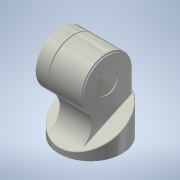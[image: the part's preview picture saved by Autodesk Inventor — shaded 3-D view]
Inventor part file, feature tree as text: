
AUTODESK INVENTOR PART (.ipt)
format: ipt  version: 2021 (Build 250183000, 183)  size: 448,512 bytes
history: native  units: mm (DEFAULTED — no unit token found)
features: sketch x9, extrude x5, hole x2, other x1, fillet x1, mirror x1, shell x1, revolve x1, pattern_circular x1
ambient origin geometry x8: Origin, YZ Plane, XZ Plane, XY Plane, X Axis, Y Axis, Z Axis, Center Point
bodies: Solid1 (feature_tree)
feature tree (22):
  other  "Center-Work Plane"
  fillet  "Chamfer"  Radius=150.0mm
  sketch  "Sketch6"  dims[d1=120.0mm d2=0.0mm d7=13.0mm d8=4.363323mm]
  extrude  "Extrusion6"  Depth=13.0mm
  mirror  "Mirror3"
  shell  "Shell1"  Thickness=4.363323mm
  hole  "Hole1"  [1 undecoded]
  hole  "Hole2"  [1 undecoded]
  extrude  "Extrusion7"  Depth=2.0mm
  extrude  "Extrusion8"  Depth=2.0mm TaperAngle=0.0deg
  extrude  "Extrusion9"  Depth=30.0mm TaperAngle=0.0deg
  extrude  "Extrusion10"  Depth=30.0mm TaperAngle=0.0deg
  revolve  "Revolution1"  [1 undecoded]
  pattern_circular  "Circular Pattern1"  Angle=90.0deg  [1 undecoded]
  sketch  "Sketch7"  dims[d9=155.0mm d10=0.0mm d11=120.0mm]
  sketch  "Sketch10"  dims[d12=90.0mm d13=128.0mm]
  sketch  "Sketch11"  dims[d14=76.0mm d15=0.0mm d19=2.0mm]
  sketch  "Sketch12"  dims[d20=4.0mm d21=2.0mm d22=0.0mm]
  sketch  "Sketch13"  dims[d25=2.0mm]
  sketch  "Sketch14"  dims[d26=50.0mm d27=6.0mm d28=4.0mm d29=2.0mm d30=14.3117mm d31=2.0mm d32=20.594885mm]
  sketch  "Sketch15"  dims[d33=50.0mm d34=6.0mm d35=4.0mm d36=2.0mm d37=14.3117mm d38=2.0mm d39=20.594885mm d40=30.0mm d41=0.0mm]
  sketch  "Sketch16"  dims[d42=30.0mm d43=0.0mm d44=30.0mm d45=0.0mm d46=30.0mm d47=0.0mm d48=90.0deg d49=150.0mm d50=360.0deg]
note: 4 required parameter values undecoded (feature->parameter linkage not recoverable at this tier; creation-order binding heuristic only, values carry confidence <= 0.55)